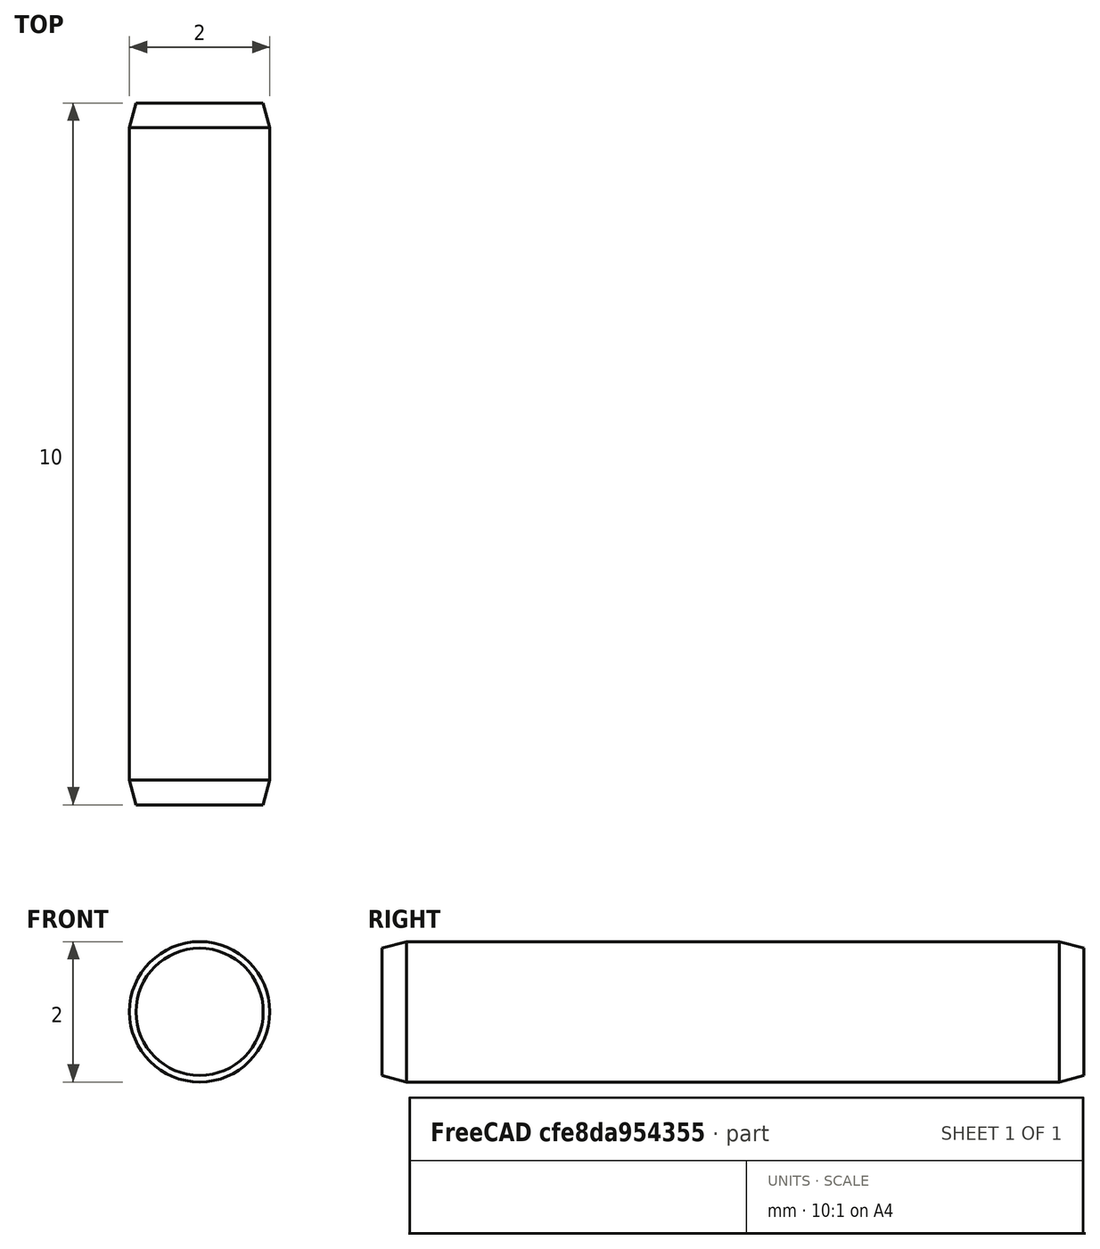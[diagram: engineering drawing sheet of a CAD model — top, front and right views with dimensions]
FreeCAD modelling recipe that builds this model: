
FCSTD DOCUMENT  (FreeCAD 0.15R4470 (Git))
Label: Zyl-Stift_ISO_2338-2x10
License: CC-BY 3.0
LicenseURL: http://creativecommons.org/licenses/by/3.0/
objects: Sketcher::SketchObject×1, PartDesign::Revolution×1
note: 3 computed .brp shape members not serialized (recipe doc carries the construction recipe); baked Part::Feature solids carry a one-line shape summary decoded from their .brp

FEATURE [Sketcher::SketchObject] Sketch
  Placement = pos=(0,0,0) rot=(0.57735,0.57735,0.57735;2.0944rad)
  sketch-geometry (7):
    g0: LineSegment StartX=0 StartY=0 StartZ=0 EndX=0 EndY=0.906218 EndZ=0
    g1: LineSegment StartX=0 StartY=0.906218 StartZ=0 EndX=0.35 EndY=1 EndZ=0
    g2: LineSegment StartX=0.35 StartY=1 StartZ=0 EndX=9.65 EndY=1 EndZ=0
    g3: LineSegment StartX=9.65 StartY=1 StartZ=0 EndX=10 EndY=0.906218 EndZ=0
    g4: LineSegment StartX=10 StartY=0.906218 StartZ=0 EndX=10 EndY=0 EndZ=0
    g5: LineSegment StartX=10 StartY=0 StartZ=0 EndX=0 EndY=0 EndZ=0
    g6: LineSegment [constr] StartX=0 StartY=0.906218 StartZ=0 EndX=10 EndY=0.906218 EndZ=0
  constraints (19):
    c: Coincident(g0,g-1)
    c: PointOnObject(g0,g-2)
    c: Coincident(g0,g1)
    c: Coincident(g1,g2)
    c: Horizontal(g2)
    c: Coincident(g2,g3)
    c: Coincident(g3,g4)
    c: Vertical(g4)
    c: Coincident(g4,g5)
    c: Coincident(g5,g-1)
    c: Horizontal(g5)
    c: Equal(g3,g1)
    c: Coincident(g6,g0)
    c: Coincident(g6,g3)
    c: Horizontal(g6)
    c: Angle(g6,g1) = 0.261799
    c: DistanceY(g-1,g1) = 1
    c: DistanceX(g5) = -10
    c: DistanceX(g1) = 0.35
FEATURE [PartDesign::Revolution] Revolution  label="Zyl-Stift ISO 2338-2x10 #"
  Angle = 360
  Axis = (0,1,0)
  Base = (0,0,0)
  Placement = pos=(0,0,0) rot=(0.57735,0.57735,0.57735;2.0944rad)
  ReferenceAxis = -> Sketch [H_Axis]
  Sketch = -> Sketch
